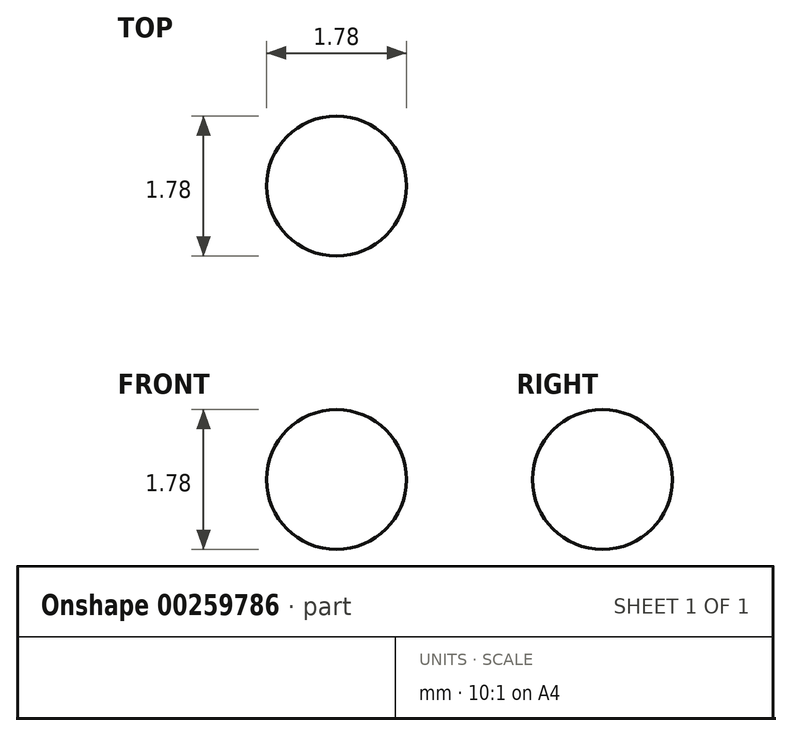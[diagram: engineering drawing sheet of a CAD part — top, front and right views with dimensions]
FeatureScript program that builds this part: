
annotation { "Feature Type Name" : "Feature", "Feature Type Description" : "" }
export const myFeature = defineFeature(function(context is Context, id is Id, definition is map)
    precondition{}
    {
        {
            var Q0;
            Q0=qCreatedBy(makeId("Top.planeOp"),FACE);
            var sketch = newSketch(context, id + "F0", { "sketchPlane" : qUnion([Q0])});
            skArc(sketch, "E0", {"start": v(0.89, 0) * mm, "mid": v(0, 0.89) * mm, "end": v(-0.89, 0) * mm});
            skLineSegment(sketch, "E1", {"start": v(-0.89, 0) * mm, "end": v(0.89, 0) * mm});
            skSolve(sketch);
        }
        {
            var Q0;
            Q0 = qSketchRegion(id + "F0", true);
            var Q1;
            Q1=sQuery(id+"F0.wireOp",EDGE,"E1");
            revolve(context, id + "F1", {"entities" : qUnion([Q0]), "axis" : qUnion([Q1]), "revolveType" : RevolveType.FULL});
        }
    });
